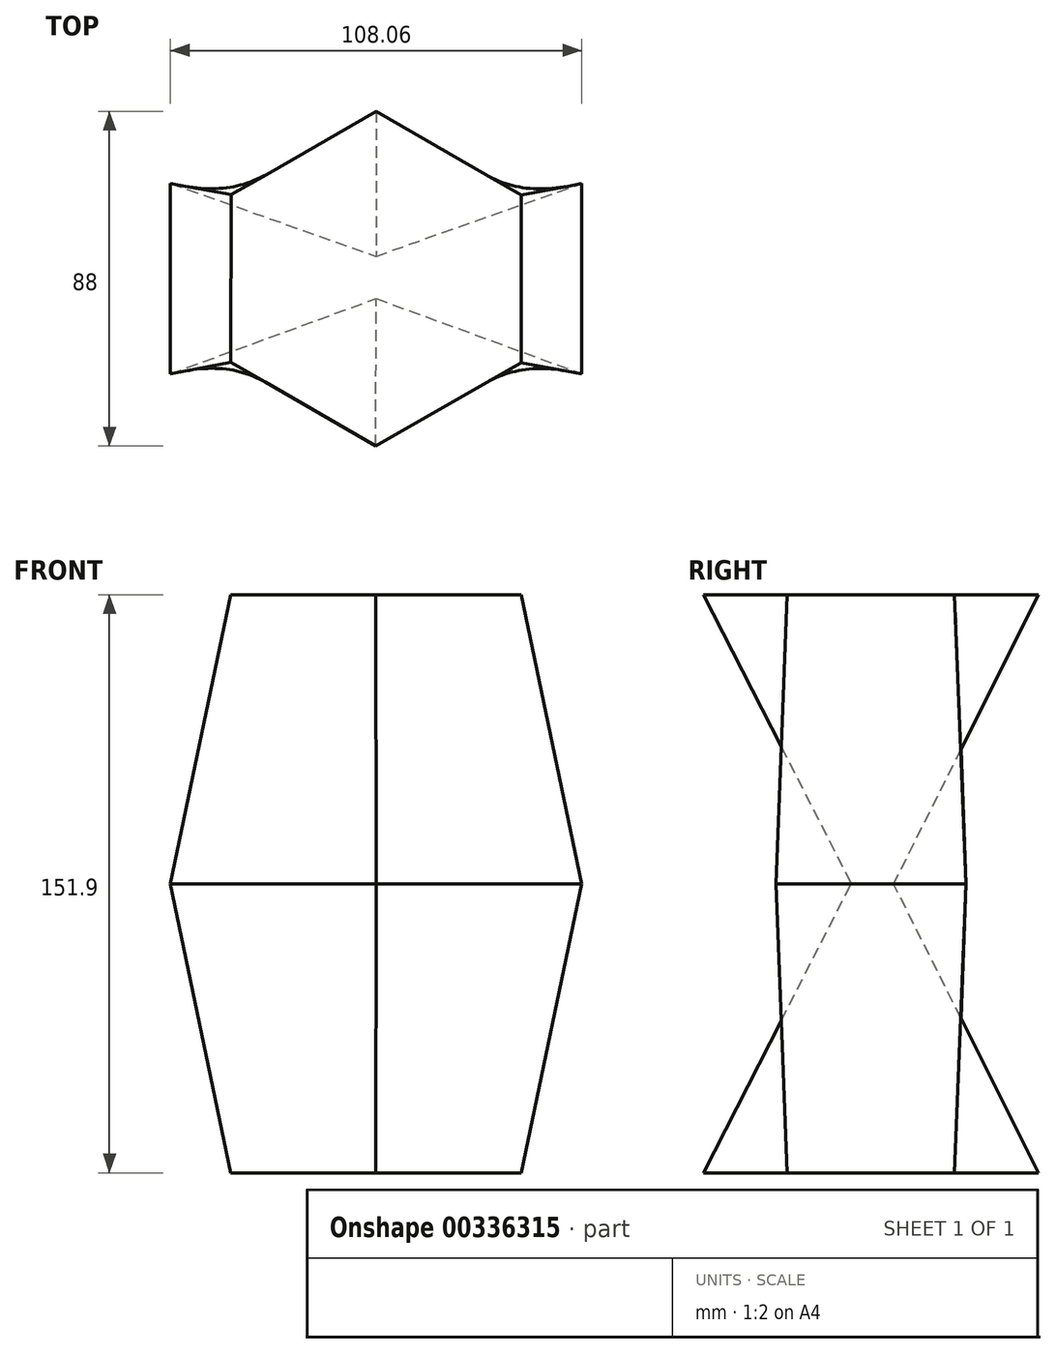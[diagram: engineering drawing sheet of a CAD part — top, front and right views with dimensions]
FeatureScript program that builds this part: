
annotation { "Feature Type Name" : "Feature", "Feature Type Description" : "" }
export const myFeature = defineFeature(function(context is Context, id is Id, definition is map)
    precondition{}
    {
        {
            var Q0;
            Q0=qCreatedBy(makeId("Top.planeOp"),FACE);
            var sketch = newSketch(context, id + "F0", { "sketchPlane" : qUnion([Q0])});
            skLineSegment(sketch, "E0.left", {"start": v(54.03, 25) * mm, "end": v(54.03, -25) * mm});
            skLineSegment(sketch, "E0.right", {"start": v(-54.03, 25) * mm, "end": v(-54.03, -25) * mm});
            skPoint(sketch, "E0.middle", {"position": v(0, 0) * mm});
            skLineSegment(sketch, "E1", {"start": v(-54.03, 25) * mm, "end": v(0, 5.9) * mm});
            skLineSegment(sketch, "E2", {"start": v(0, 5.9) * mm, "end": v(54.03, 25) * mm});
            skLineSegment(sketch, "E3", {"start": v(-54.03, -25) * mm, "end": v(0, -5.22) * mm});
            skLineSegment(sketch, "E4", {"start": v(0, -5.22) * mm, "end": v(54.03, -25) * mm});
            skSolve(sketch);
        }
        {
            var Q0;
            Q0=qCreatedBy(makeId("Top.planeOp"),FACE);
            cPlane(context, id + "F1", {"entities" : qUnion([Q0]), "cplaneType" : CPlaneType.OFFSET, "offset" : 75.95 * mm, "width" : 152.4 * mm, "height" : 152.4 * mm});
        }
        {
            var Q0;
            Q0=qCreatedBy(id+"F1.planeOp",FACE);
            var sketch = newSketch(context, id + "F2", { "sketchPlane" : qUnion([Q0])});
            skCircle(sketch, "E5.cCircle", {"center": v(0, 0) * mm, "radius": 38.1 * mm, "construction": true});
            skLineSegment(sketch, "E5.0", {"start": v(0.08, 44) * mm, "end": v(38.15, 21.93) * mm});
            skLineSegment(sketch, "E5.1", {"start": v(38.15, 21.93) * mm, "end": v(38.07, -22.07) * mm});
            skLineSegment(sketch, "E5.2", {"start": v(38.07, -22.07) * mm, "end": v(-0.08, -44) * mm});
            skLineSegment(sketch, "E5.3", {"start": v(-0.08, -44) * mm, "end": v(-38.15, -21.93) * mm});
            skLineSegment(sketch, "E5.4", {"start": v(-38.15, -21.93) * mm, "end": v(-38.07, 22.07) * mm});
            skLineSegment(sketch, "E5.5", {"start": v(-38.07, 22.07) * mm, "end": v(0.08, 44) * mm});
            skPoint(sketch, "E5.0.midPoint", {"position": v(19.11, 32.97) * mm});
            skSolve(sketch);
        }
        {
            var Q0;
            Q0=makeQuery(id+"F2.imprint","IMPRINT",FACE,{"disambiguationData":[TD([[makeQuery(id+"F2.imprint","IMPRINT",EDGE,{"derivedFrom":sQuery(id+"F2.wireOp",EDGE,"E5.0")}),-1.0]])]});
            var Q1;
            Q1=makeQuery(id+"F0.imprint","IMPRINT",FACE,{"disambiguationData":[TD([[makeQuery(id+"F0.imprint","IMPRINT",EDGE,{"derivedFrom":sQuery(id+"F0.wireOp",EDGE,"E0.left")}),-1.0]])]});
            loft(context, id + "F3", {"sheetProfilesArray" : [{ "sheetProfileEntities" : qUnion([Q0]) }, { "sheetProfileEntities" : qUnion([Q1]) }]});
        }
        {
            var Q0;
            Q0=makeQuery(id+"F3.opLoft","SWEPT_BODY",BODY,{"disambiguationData":[OSD([makeQuery(id+"F0.imprint","IMPRINT",FACE,{"disambiguationData":[TD([[makeQuery(id+"F0.imprint","IMPRINT",EDGE,{"derivedFrom":sQuery(id+"F0.wireOp",EDGE,"E0.left")}),-1.0]])]}),makeQuery(id+"F2.imprint","IMPRINT",FACE,{"disambiguationData":[TD([[makeQuery(id+"F2.imprint","IMPRINT",EDGE,{"derivedFrom":sQuery(id+"F2.wireOp",EDGE,"E5.0")}),-1.0]])]})])]});
            var Q1;
            Q1=qCreatedBy(makeId("Top.planeOp"),FACE);
            mirror(context, id + "F4", {"operationType" : NewBodyOperationType.ADD, "entities" : qUnion([Q0]), "mirrorPlane" : qUnion([Q1])});
        }
    });
